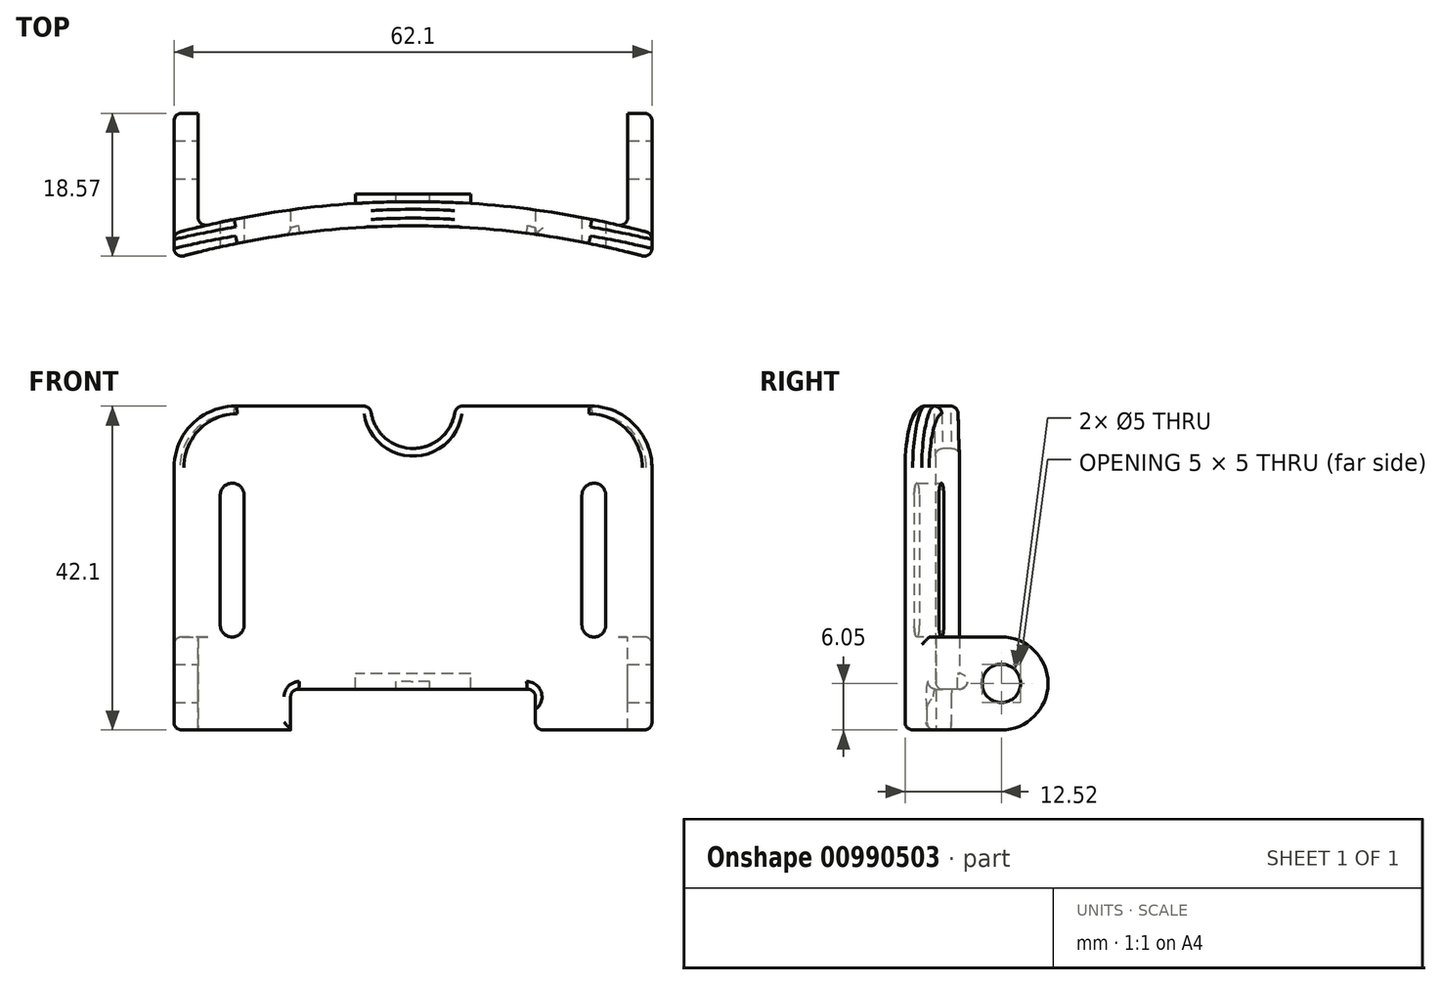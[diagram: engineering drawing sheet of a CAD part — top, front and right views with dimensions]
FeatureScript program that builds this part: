
annotation { "Feature Type Name" : "Feature", "Feature Type Description" : "" }
export const myFeature = defineFeature(function(context is Context, id is Id, definition is map)
    precondition{}
    {
        {
            var Q0;
            Q0=qCreatedBy(makeId("Top.planeOp"),FACE);
            var sketch = newSketch(context, id + "F0", { "sketchPlane" : qUnion([Q0])});
            skArc(sketch, "E0", {"start": v(8.06, 0) * mm, "mid": v(-23, 4.25) * mm, "end": v(-54.04, 0) * mm});
            skLineSegment(sketch, "E1", {"start": v(8.06, 0) * mm, "end": v(8.06, 18.88) * mm});
            skLineSegment(sketch, "E2", {"start": v(8.06, 18.88) * mm, "end": v(4.92, 18.88) * mm});
            skLineSegment(sketch, "E3", {"start": v(-54.04, 0) * mm, "end": v(-54.04, 18.88) * mm});
            skLineSegment(sketch, "E4", {"start": v(-54.04, 18.88) * mm, "end": v(-50.9, 18.88) * mm});
            skArc(sketch, "E5.0", {"start": v(8.06, 3.26) * mm, "mid": v(-23, 7.39) * mm, "end": v(-54.04, 3.26) * mm});
            skLineSegment(sketch, "E6", {"start": v(-50.9, 18.88) * mm, "end": v(-50.9, 4.06) * mm});
            skLineSegment(sketch, "E7", {"start": v(4.92, 18.88) * mm, "end": v(4.92, 4.06) * mm});
            skSolve(sketch);
        }
        {
            var Q0;
            Q0 = qSketchRegion(id + "F0", true);
            extrude(context, id + "F1", {"entities" : qUnion([Q0]), "depth" : 12.1 * mm, "offsetDistance" : 25 * mm});
        }
        {
            var Q0;
            {var subQ5=sQuery(id+"F0.wireOp",EDGE,"E0");Q0=makeQuery(id+"F0.imprint","IMPRINT",FACE,{"disambiguationData":[TD([[makeQuery(id+"F0.imprint","IMPRINT",EDGE,{"derivedFrom":subQ5}),-1.0]])]});}
            extrude(context, id + "F2", {"entities" : qUnion([Q0]), "operationType" : NewBodyOperationType.ADD, "depth" : 42.1 * mm, "offsetDistance" : 25 * mm});
        }
        {
            var Q0;
            Q0=makeQuery(id+"F1.opExtrude","CAP_EDGE",EDGE,{"disambiguationData":[OSD([sQuery(id+"F0.wireOp",EDGE,"E4")])],"isStart":false});
            var Q1;
            Q1=makeQuery(id+"F1.opExtrude","CAP_EDGE",EDGE,{"disambiguationData":[OSD([sQuery(id+"F0.wireOp",EDGE,"E4")])],"isStart":true});
            var Q2;
            Q2=makeQuery(id+"F1.opExtrude","CAP_EDGE",EDGE,{"disambiguationData":[OSD([sQuery(id+"F0.wireOp",EDGE,"E2")])],"isStart":true});
            var Q3;
            Q3=makeQuery(id+"F1.opExtrude","CAP_EDGE",EDGE,{"disambiguationData":[OSD([sQuery(id+"F0.wireOp",EDGE,"E2")])],"isStart":false});
            fillet(context, id + "F3", {"entities" : qUnion([Q0, Q1, Q2, Q3]), "radius" : 6.05 * mm, "tangentPropagation" : true, "allowEdgeOverflow" : false});
        }
        {
            var Q0;
            Q0=makeQuery(id+"F1.opExtrude","SWEPT_EDGE",EDGE,{"disambiguationData":[OSD([sQuery(id+"F0.wireOp",EDGE,"E5.0"),sQuery(id+"F0.wireOp",EDGE,"E7")])]});
            var Q1;
            Q1=makeQuery(id+"F1.opExtrude","SWEPT_EDGE",EDGE,{"disambiguationData":[OSD([sQuery(id+"F0.wireOp",EDGE,"E5.0"),sQuery(id+"F0.wireOp",EDGE,"E6")])]});
            var Q2;
            {var subQ0=sQuery(id+"F0.wireOp",EDGE,"E1");var subQ1=sQuery(id+"F0.wireOp",EDGE,"E0");Q2=makeQuery(id+"F2.boolean.opBoolean","MERGE",EDGE,{"derivedFrom":[makeQuery(id+"F1.opExtrude","SWEPT_EDGE",EDGE,{"disambiguationData":[OSD([subQ1,subQ0])]}),makeQuery(id+"F2.opExtrude","SWEPT_EDGE",EDGE,{"disambiguationData":[OSD([subQ1,subQ0])]})]});}
            var Q3;
            {var subQ0=sQuery(id+"F0.wireOp",EDGE,"E3");var subQ1=sQuery(id+"F0.wireOp",EDGE,"E0");Q3=makeQuery(id+"F2.boolean.opBoolean","MERGE",EDGE,{"derivedFrom":[makeQuery(id+"F1.opExtrude","SWEPT_EDGE",EDGE,{"disambiguationData":[OSD([subQ1,subQ0])]}),makeQuery(id+"F2.opExtrude","SWEPT_EDGE",EDGE,{"disambiguationData":[OSD([subQ1,subQ0])]})]});}
            var Q4;
            Q4=makeQuery(id+"F2.opExtrude","SWEPT_EDGE",EDGE,{"disambiguationData":[OSD([sQuery(id+"F0.wireOp",EDGE,"E1"),sQuery(id+"F0.wireOp",EDGE,"E5.0")])]});
            var Q5;
            Q5=makeQuery(id+"F2.opExtrude","SWEPT_EDGE",EDGE,{"disambiguationData":[OSD([sQuery(id+"F0.wireOp",EDGE,"E3"),sQuery(id+"F0.wireOp",EDGE,"E5.0")])]});
            var Q6;
            Q6=makeQuery(id+"F1.opExtrude","CAP_EDGE",EDGE,{"disambiguationData":[OSD([sQuery(id+"F0.wireOp",EDGE,"E3")])],"isStart":false});
            var Q7;
            {var subQ0=sQuery(id+"F0.wireOp",EDGE,"E1");Q7=makeQuery(id+"F3.opFillet","BLEND_EDGE",EDGE,{"blendedFrom":[makeQuery(id+"F1.opExtrude","CAP_EDGE",EDGE,{"disambiguationData":[OSD([sQuery(id+"F0.wireOp",EDGE,"E2")])],"isStart":true}),makeQuery(id+"F2.boolean.opBoolean","MERGE",FACE,{"derivedFrom":[makeQuery(id+"F1.opExtrude","SWEPT_FACE",FACE,{"disambiguationData":[OSD([subQ0])]}),makeQuery(id+"F2.opExtrude","SWEPT_FACE",FACE,{"disambiguationData":[OSD([subQ0])]})]})],"blendedInto":[makeQuery(id+"F2.boolean.opBoolean","MERGE",FACE,{"derivedFrom":[makeQuery(id+"F1.opExtrude","SWEPT_FACE",FACE,{"disambiguationData":[OSD([subQ0])]}),makeQuery(id+"F2.opExtrude","SWEPT_FACE",FACE,{"disambiguationData":[OSD([subQ0])]})]})]});}
            var Q8;
            Q8=makeQuery(id+"F2.opExtrude","CAP_EDGE",EDGE,{"disambiguationData":[OSD([sQuery(id+"F0.wireOp",EDGE,"E0")])],"isStart":false});
            var Q9;
            Q9=makeQuery(id+"F2.opExtrude","CAP_EDGE",EDGE,{"disambiguationData":[OSD([sQuery(id+"F0.wireOp",EDGE,"E5.0")])],"isStart":false});
            fillet(context, id + "F4", {"entities" : qUnion([Q0, Q1, Q2, Q3, Q4, Q5, Q6, Q7, Q8, Q9]), "radius" : 1 * mm, "tangentPropagation" : true, "allowEdgeOverflow" : false});
        }
        {
            var Q0;
            {var subQ0=sQuery(id+"F0.wireOp",EDGE,"E1");var subQ1=sQuery(id+"F0.wireOp",EDGE,"E0");Q0=makeQuery(id+"F4.opFillet","BLEND_VERTEX",VERTEX,{"blendedFrom":[makeQuery(id+"F2.boolean.opBoolean","MERGE",EDGE,{"derivedFrom":[makeQuery(id+"F1.opExtrude","SWEPT_EDGE",EDGE,{"disambiguationData":[OSD([subQ1,subQ0])]}),makeQuery(id+"F2.opExtrude","SWEPT_EDGE",EDGE,{"disambiguationData":[OSD([subQ1,subQ0])]})]}),makeQuery(id+"F2.boolean.opBoolean","MERGE",FACE,{"derivedFrom":[makeQuery(id+"F1.opExtrude","SWEPT_FACE",FACE,{"disambiguationData":[OSD([subQ1])]}),makeQuery(id+"F2.opExtrude","SWEPT_FACE",FACE,{"disambiguationData":[OSD([subQ1])]})]}),makeQuery(id+"F1.opExtrude","CAP_FACE",FACE,{"disambiguationData":[OSD([subQ1,subQ0,sQuery(id+"F0.wireOp",EDGE,"E2"),sQuery(id+"F0.wireOp",EDGE,"E3"),sQuery(id+"F0.wireOp",EDGE,"E4"),sQuery(id+"F0.wireOp",EDGE,"E5.0"),sQuery(id+"F0.wireOp",EDGE,"E6"),sQuery(id+"F0.wireOp",EDGE,"E7")])],"isStart":true})],"blendedInto":[makeQuery(id+"F2.boolean.opBoolean","MERGE",FACE,{"derivedFrom":[makeQuery(id+"F1.opExtrude","SWEPT_FACE",FACE,{"disambiguationData":[OSD([subQ1])]}),makeQuery(id+"F2.opExtrude","SWEPT_FACE",FACE,{"disambiguationData":[OSD([subQ1])]})]}),makeQuery(id+"F1.opExtrude","CAP_FACE",FACE,{"disambiguationData":[OSD([subQ1,subQ0,sQuery(id+"F0.wireOp",EDGE,"E2"),sQuery(id+"F0.wireOp",EDGE,"E3"),sQuery(id+"F0.wireOp",EDGE,"E4"),sQuery(id+"F0.wireOp",EDGE,"E5.0"),sQuery(id+"F0.wireOp",EDGE,"E6"),sQuery(id+"F0.wireOp",EDGE,"E7")])],"isStart":true})]});}
            var Q1;
            {var subQ0=sQuery(id+"F0.wireOp",EDGE,"E3");var subQ1=sQuery(id+"F0.wireOp",EDGE,"E0");Q1=makeQuery(id+"F4.opFillet","BLEND_VERTEX",VERTEX,{"blendedFrom":[makeQuery(id+"F2.boolean.opBoolean","MERGE",EDGE,{"derivedFrom":[makeQuery(id+"F1.opExtrude","SWEPT_EDGE",EDGE,{"disambiguationData":[OSD([subQ1,subQ0])]}),makeQuery(id+"F2.opExtrude","SWEPT_EDGE",EDGE,{"disambiguationData":[OSD([subQ1,subQ0])]})]}),makeQuery(id+"F2.boolean.opBoolean","MERGE",FACE,{"derivedFrom":[makeQuery(id+"F1.opExtrude","SWEPT_FACE",FACE,{"disambiguationData":[OSD([subQ1])]}),makeQuery(id+"F2.opExtrude","SWEPT_FACE",FACE,{"disambiguationData":[OSD([subQ1])]})]}),makeQuery(id+"F1.opExtrude","CAP_FACE",FACE,{"disambiguationData":[OSD([subQ1,sQuery(id+"F0.wireOp",EDGE,"E1"),sQuery(id+"F0.wireOp",EDGE,"E2"),subQ0,sQuery(id+"F0.wireOp",EDGE,"E4"),sQuery(id+"F0.wireOp",EDGE,"E5.0"),sQuery(id+"F0.wireOp",EDGE,"E6"),sQuery(id+"F0.wireOp",EDGE,"E7")])],"isStart":true})],"blendedInto":[makeQuery(id+"F2.boolean.opBoolean","MERGE",FACE,{"derivedFrom":[makeQuery(id+"F1.opExtrude","SWEPT_FACE",FACE,{"disambiguationData":[OSD([subQ1])]}),makeQuery(id+"F2.opExtrude","SWEPT_FACE",FACE,{"disambiguationData":[OSD([subQ1])]})]}),makeQuery(id+"F1.opExtrude","CAP_FACE",FACE,{"disambiguationData":[OSD([subQ1,sQuery(id+"F0.wireOp",EDGE,"E1"),sQuery(id+"F0.wireOp",EDGE,"E2"),subQ0,sQuery(id+"F0.wireOp",EDGE,"E4"),sQuery(id+"F0.wireOp",EDGE,"E5.0"),sQuery(id+"F0.wireOp",EDGE,"E6"),sQuery(id+"F0.wireOp",EDGE,"E7")])],"isStart":true})]});}
            var Q2;
            {var subQ0=sQuery(id+"F0.wireOp",EDGE,"E0");var subQ1=sQuery(id+"F0.wireOp",EDGE,"E3");Q2=makeQuery(id+"F4.opFillet","BLEND_VERTEX",VERTEX,{"blendedFrom":[makeQuery(id+"F2.opExtrude","CAP_EDGE",EDGE,{"disambiguationData":[OSD([subQ0])],"isStart":false}),makeQuery(id+"F2.boolean.opBoolean","MERGE",EDGE,{"derivedFrom":[makeQuery(id+"F1.opExtrude","SWEPT_EDGE",EDGE,{"disambiguationData":[OSD([subQ0,subQ1])]}),makeQuery(id+"F2.opExtrude","SWEPT_EDGE",EDGE,{"disambiguationData":[OSD([subQ0,subQ1])]})]}),makeQuery(id+"F2.boolean.opBoolean","MERGE",FACE,{"derivedFrom":[makeQuery(id+"F1.opExtrude","SWEPT_FACE",FACE,{"disambiguationData":[OSD([subQ0])]}),makeQuery(id+"F2.opExtrude","SWEPT_FACE",FACE,{"disambiguationData":[OSD([subQ0])]})]})],"blendedInto":[makeQuery(id+"F2.boolean.opBoolean","MERGE",FACE,{"derivedFrom":[makeQuery(id+"F1.opExtrude","SWEPT_FACE",FACE,{"disambiguationData":[OSD([subQ0])]}),makeQuery(id+"F2.opExtrude","SWEPT_FACE",FACE,{"disambiguationData":[OSD([subQ0])]})]})]});}
            cPlane(context, id + "F5", {"entities" : qUnion([Q0, Q1, Q2]), "cplaneType" : CPlaneType.THREE_POINT, "offset" : 25 * mm, "width" : 150 * mm, "height" : 150 * mm});
        }
        {
            var Q0;
            Q0=qCreatedBy(id+"F5.planeOp",FACE);
            var sketch = newSketch(context, id + "F6", { "sketchPlane" : qUnion([Q0])});
            skPoint(sketch, "E8.0", {"position": v(-23, 0) * mm});
            skLineSegment(sketch, "E9.0", {"start": v(-54.04, 0) * mm, "end": v(-54.04, 42.1) * mm, "construction": true});
            skLineSegment(sketch, "E10.0", {"start": v(8.06, 42.1) * mm, "end": v(8.06, 0) * mm, "construction": true});
            skLineSegment(sketch, "E11", {"start": v(-23, 42.1) * mm, "end": v(-23, 0) * mm, "construction": true});
            skLineSegment(sketch, "E12.bottom", {"start": v(-7.1, 0) * mm, "end": v(-38.9, 0) * mm});
            skLineSegment(sketch, "E12.top", {"start": v(-7.1, 5.3) * mm, "end": v(-38.9, 5.3) * mm});
            skLineSegment(sketch, "E12.left", {"start": v(-7.1, 0) * mm, "end": v(-7.1, 5.3) * mm});
            skLineSegment(sketch, "E12.right", {"start": v(-38.9, 0) * mm, "end": v(-38.9, 5.3) * mm});
            skLineSegment(sketch, "E13.bottom", {"start": v(2.06, 32.08) * mm, "end": v(-1.04, 32.08) * mm});
            skLineSegment(sketch, "E13.top", {"start": v(2.06, 12.08) * mm, "end": v(-1.04, 12.08) * mm});
            skLineSegment(sketch, "E13.left", {"start": v(2.06, 32.08) * mm, "end": v(2.06, 12.08) * mm});
            skLineSegment(sketch, "E13.right", {"start": v(-1.04, 32.08) * mm, "end": v(-1.04, 12.08) * mm});
            skLineSegment(sketch, "E14.MirrorCS", {"start": v(-48.04, 32.08) * mm, "end": v(-48.04, 12.08) * mm});
            skLineSegment(sketch, "E15.MirrorCS", {"start": v(-44.94, 32.08) * mm, "end": v(-44.94, 12.08) * mm});
            skLineSegment(sketch, "E16.MirrorCS", {"start": v(-48.04, 12.08) * mm, "end": v(-44.94, 12.08) * mm});
            skLineSegment(sketch, "E17.MirrorCS", {"start": v(-48.04, 32.08) * mm, "end": v(-44.94, 32.08) * mm});
            skCircle(sketch, "E18", {"center": v(-23, 42.1) * mm, "radius": 5.5 * mm});
            skSolve(sketch);
        }
        {
            var Q0;
            Q0 = qSketchRegion(id + "F6", true);
            extrude(context, id + "F7", {"entities" : qUnion([Q0]), "operationType" : NewBodyOperationType.REMOVE, "endBound" : BoundingType.THROUGH_ALL, "oppositeDirection" : true, "depth" : 25 * mm, "offsetDistance" : 25 * mm});
        }
        {
            var Q0;
            Q0=makeQuery(id+"F7.boolean.opBoolean","COPY",EDGE,{"derivedFrom":makeQuery(id+"F7.opExtrude","SWEPT_EDGE",EDGE,{"disambiguationData":[OSD([sQuery(id+"F6.wireOp",EDGE,"E12.bottom"),sQuery(id+"F6.wireOp",EDGE,"E12.left")])]})});
            var Q1;
            Q1=makeQuery(id+"F7.boolean.opBoolean","COPY",EDGE,{"derivedFrom":makeQuery(id+"F7.opExtrude","SWEPT_EDGE",EDGE,{"disambiguationData":[OSD([sQuery(id+"F6.wireOp",EDGE,"E12.top"),sQuery(id+"F6.wireOp",EDGE,"E12.left")])]})});
            var Q2;
            Q2=makeQuery(id+"F7.boolean.opBoolean","COPY",EDGE,{"derivedFrom":makeQuery(id+"F7.opExtrude","SWEPT_EDGE",EDGE,{"disambiguationData":[OSD([sQuery(id+"F6.wireOp",EDGE,"E12.top"),sQuery(id+"F6.wireOp",EDGE,"E12.right")])]})});
            var Q3;
            Q3=makeQuery(id+"F7.boolean.opBoolean","COPY",EDGE,{"derivedFrom":makeQuery(id+"F7.opExtrude","SWEPT_EDGE",EDGE,{"disambiguationData":[OSD([sQuery(id+"F6.wireOp",EDGE,"E12.bottom"),sQuery(id+"F6.wireOp",EDGE,"E12.right")])]})});
            var Q4;
            Q4=makeQuery(id+"F7.boolean.opBoolean","INTERSECT",EDGE,{"disambiguationData":[OD(0.0)],"derivedFrom":[makeQuery(id+"F2.opExtrude","CAP_FACE",FACE,{"disambiguationData":[OSD([sQuery(id+"F0.wireOp",EDGE,"E0"),sQuery(id+"F0.wireOp",EDGE,"E1"),sQuery(id+"F0.wireOp",EDGE,"E3"),sQuery(id+"F0.wireOp",EDGE,"E5.0")])],"isStart":false}),makeQuery(id+"F7.opExtrude","SWEPT_FACE",FACE,{"disambiguationData":[OSD([sQuery(id+"F6.wireOp",EDGE,"E18")])]})]});
            var Q5;
            Q5=makeQuery(id+"F7.boolean.opBoolean","INTERSECT",EDGE,{"disambiguationData":[OD(1.0)],"derivedFrom":[makeQuery(id+"F2.opExtrude","CAP_FACE",FACE,{"disambiguationData":[OSD([sQuery(id+"F0.wireOp",EDGE,"E0"),sQuery(id+"F0.wireOp",EDGE,"E1"),sQuery(id+"F0.wireOp",EDGE,"E3"),sQuery(id+"F0.wireOp",EDGE,"E5.0")])],"isStart":false}),makeQuery(id+"F7.opExtrude","SWEPT_FACE",FACE,{"disambiguationData":[OSD([sQuery(id+"F6.wireOp",EDGE,"E18")])]})]});
            var Q6;
            {var subQ1=sQuery(id+"F0.wireOp",EDGE,"E0");Q6=makeQuery(id+"F7.boolean.opBoolean","SPLIT",EDGE,{"disambiguationData":[TD([makeQuery(id+"F7.opExtrude","SWEPT_FACE",FACE,{"disambiguationData":[OSD([sQuery(id+"F6.wireOp",EDGE,"E12.right")])]})])],"derivedFrom":makeQuery(id+"F1.opExtrude","CAP_EDGE",EDGE,{"disambiguationData":[OSD([subQ1])],"isStart":true})});}
            var Q7;
            {var subQ0=sQuery(id+"F0.wireOp",EDGE,"E0");Q7=makeQuery(id+"F7.boolean.opBoolean","INTERSECT",EDGE,{"derivedFrom":[makeQuery(id+"F2.boolean.opBoolean","MERGE",FACE,{"derivedFrom":[makeQuery(id+"F1.opExtrude","SWEPT_FACE",FACE,{"disambiguationData":[OSD([subQ0])]}),makeQuery(id+"F2.opExtrude","SWEPT_FACE",FACE,{"disambiguationData":[OSD([subQ0])]})]}),makeQuery(id+"F7.opExtrude","SWEPT_FACE",FACE,{"disambiguationData":[OSD([sQuery(id+"F6.wireOp",EDGE,"E12.right")])]})]});}
            var Q8;
            {var subQ0=sQuery(id+"F0.wireOp",EDGE,"E0");Q8=makeQuery(id+"F7.boolean.opBoolean","INTERSECT",EDGE,{"derivedFrom":[makeQuery(id+"F2.boolean.opBoolean","MERGE",FACE,{"derivedFrom":[makeQuery(id+"F1.opExtrude","SWEPT_FACE",FACE,{"disambiguationData":[OSD([subQ0])]}),makeQuery(id+"F2.opExtrude","SWEPT_FACE",FACE,{"disambiguationData":[OSD([subQ0])]})]}),makeQuery(id+"F7.opExtrude","SWEPT_FACE",FACE,{"disambiguationData":[OSD([sQuery(id+"F6.wireOp",EDGE,"E12.top")])]})]});}
            var Q9;
            {var subQ1=sQuery(id+"F0.wireOp",EDGE,"E0");Q9=makeQuery(id+"F7.boolean.opBoolean","SPLIT",EDGE,{"disambiguationData":[TD([makeQuery(id+"F7.opExtrude","SWEPT_FACE",FACE,{"disambiguationData":[OSD([sQuery(id+"F6.wireOp",EDGE,"E12.left")])]})])],"derivedFrom":makeQuery(id+"F1.opExtrude","CAP_EDGE",EDGE,{"disambiguationData":[OSD([subQ1])],"isStart":true})});}
            fillet(context, id + "F8", {"entities" : qUnion([Q0, Q1, Q2, Q3, Q4, Q5, Q6, Q7, Q8, Q9]), "radius" : 1 * mm, "tangentPropagation" : true, "allowEdgeOverflow" : false});
        }
        {
            var Q0;
            Q0=makeQuery(id+"F7.boolean.opBoolean","COPY",EDGE,{"derivedFrom":makeQuery(id+"F7.opExtrude","SWEPT_EDGE",EDGE,{"disambiguationData":[OSD([sQuery(id+"F6.wireOp",EDGE,"E15.MirrorCS"),sQuery(id+"F6.wireOp",EDGE,"E17.MirrorCS")])]})});
            var Q1;
            Q1=makeQuery(id+"F7.boolean.opBoolean","COPY",EDGE,{"derivedFrom":makeQuery(id+"F7.opExtrude","SWEPT_EDGE",EDGE,{"disambiguationData":[OSD([sQuery(id+"F6.wireOp",EDGE,"E13.bottom"),sQuery(id+"F6.wireOp",EDGE,"E13.left")])]})});
            var Q2;
            Q2=makeQuery(id+"F7.boolean.opBoolean","COPY",EDGE,{"derivedFrom":makeQuery(id+"F7.opExtrude","SWEPT_EDGE",EDGE,{"disambiguationData":[OSD([sQuery(id+"F6.wireOp",EDGE,"E13.bottom"),sQuery(id+"F6.wireOp",EDGE,"E13.right")])]})});
            var Q3;
            Q3=makeQuery(id+"F7.boolean.opBoolean","COPY",EDGE,{"derivedFrom":makeQuery(id+"F7.opExtrude","SWEPT_EDGE",EDGE,{"disambiguationData":[OSD([sQuery(id+"F6.wireOp",EDGE,"E14.MirrorCS"),sQuery(id+"F6.wireOp",EDGE,"E17.MirrorCS")])]})});
            var Q4;
            Q4=makeQuery(id+"F7.boolean.opBoolean","COPY",EDGE,{"derivedFrom":makeQuery(id+"F7.opExtrude","SWEPT_EDGE",EDGE,{"disambiguationData":[OSD([sQuery(id+"F6.wireOp",EDGE,"E15.MirrorCS"),sQuery(id+"F6.wireOp",EDGE,"E16.MirrorCS")])]})});
            var Q5;
            Q5=makeQuery(id+"F7.boolean.opBoolean","COPY",EDGE,{"derivedFrom":makeQuery(id+"F7.opExtrude","SWEPT_EDGE",EDGE,{"disambiguationData":[OSD([sQuery(id+"F6.wireOp",EDGE,"E13.top"),sQuery(id+"F6.wireOp",EDGE,"E13.left")])]})});
            var Q6;
            Q6=makeQuery(id+"F7.boolean.opBoolean","COPY",EDGE,{"derivedFrom":makeQuery(id+"F7.opExtrude","SWEPT_EDGE",EDGE,{"disambiguationData":[OSD([sQuery(id+"F6.wireOp",EDGE,"E13.top"),sQuery(id+"F6.wireOp",EDGE,"E13.right")])]})});
            var Q7;
            Q7=makeQuery(id+"F7.boolean.opBoolean","COPY",EDGE,{"derivedFrom":makeQuery(id+"F7.opExtrude","SWEPT_EDGE",EDGE,{"disambiguationData":[OSD([sQuery(id+"F6.wireOp",EDGE,"E14.MirrorCS"),sQuery(id+"F6.wireOp",EDGE,"E16.MirrorCS")])]})});
            fillet(context, id + "F9", {"entities" : qUnion([Q0, Q1, Q2, Q3, Q4, Q5, Q6, Q7]), "radius" : 1.55 * mm, "tangentPropagation" : true, "allowEdgeOverflow" : false});
        }
        {
            var Q0;
            Q0=makeQuery(id+"F1.opExtrude","SWEPT_FACE",FACE,{"disambiguationData":[OSD([sQuery(id+"F0.wireOp",EDGE,"E7")])]});
            var sketch = newSketch(context, id + "F10", { "sketchPlane" : qUnion([Q0])});
            skPoint(sketch, "E19.0", {"position": v(-18.88, 6.05) * mm});
            skLineSegment(sketch, "E20", {"start": v(-18.88, 6.05) * mm, "end": v(2.29, 6.05) * mm, "construction": true});
            skCircle(sketch, "E21", {"center": v(-12.83, 6.05) * mm, "radius": 2.5 * mm});
            skSolve(sketch);
        }
        {
            var Q0;
            Q0 = qSketchRegion(id + "F10", true);
            extrude(context, id + "F11", {"entities" : qUnion([Q0]), "operationType" : NewBodyOperationType.REMOVE, "endBound" : BoundingType.SYMMETRIC, "depth" : 153.6 * mm, "offsetDistance" : 25 * mm});
        }
        {
            var Q0;
            Q0=makeQuery(id+"F2.opExtrude","CAP_EDGE",EDGE,{"disambiguationData":[OSD([sQuery(id+"F0.wireOp",EDGE,"E3")])],"isStart":false});
            var Q1;
            Q1=makeQuery(id+"F2.opExtrude","CAP_EDGE",EDGE,{"disambiguationData":[OSD([sQuery(id+"F0.wireOp",EDGE,"E1")])],"isStart":false});
            fillet(context, id + "F12", {"entities" : qUnion([Q0, Q1]), "radius" : 8 * mm, "tangentPropagation" : true, "allowEdgeOverflow" : false});
        }
        {
            var Q0;
            {var subQ0=sQuery(id+"F0.wireOp",EDGE,"E5.0");Q0=makeQuery(id+"F8.opFillet","BLEND_EDGE",EDGE,{"blendedFrom":[makeQuery(id+"F7.boolean.opBoolean","COPY",EDGE,{"derivedFrom":makeQuery(id+"F7.opExtrude","SWEPT_EDGE",EDGE,{"disambiguationData":[OSD([sQuery(id+"F6.wireOp",EDGE,"E12.top"),sQuery(id+"F6.wireOp",EDGE,"E12.left")])]})}),makeQuery(id+"F2.boolean.opBoolean","MERGE",FACE,{"derivedFrom":[makeQuery(id+"F1.opExtrude","SWEPT_FACE",FACE,{"disambiguationData":[OSD([subQ0])]}),makeQuery(id+"F2.opExtrude","SWEPT_FACE",FACE,{"disambiguationData":[OSD([subQ0])]})]})],"blendedInto":[makeQuery(id+"F2.boolean.opBoolean","MERGE",FACE,{"derivedFrom":[makeQuery(id+"F1.opExtrude","SWEPT_FACE",FACE,{"disambiguationData":[OSD([subQ0])]}),makeQuery(id+"F2.opExtrude","SWEPT_FACE",FACE,{"disambiguationData":[OSD([subQ0])]})]})]});}
            cPoint(context, id + "F13", {"entities" : qUnion([Q0]), "parameter" : 0.5});
        }
        {
            var Q0;
            {var subQ0=sQuery(id+"F0.wireOp",EDGE,"E5.0");Q0=makeQuery(id+"F8.opFillet","BLEND_EDGE",EDGE,{"blendedFrom":[makeQuery(id+"F7.boolean.opBoolean","COPY",EDGE,{"derivedFrom":makeQuery(id+"F7.opExtrude","SWEPT_EDGE",EDGE,{"disambiguationData":[OSD([sQuery(id+"F6.wireOp",EDGE,"E12.top"),sQuery(id+"F6.wireOp",EDGE,"E12.right")])]})}),makeQuery(id+"F2.boolean.opBoolean","MERGE",FACE,{"derivedFrom":[makeQuery(id+"F1.opExtrude","SWEPT_FACE",FACE,{"disambiguationData":[OSD([subQ0])]}),makeQuery(id+"F2.opExtrude","SWEPT_FACE",FACE,{"disambiguationData":[OSD([subQ0])]})]})],"blendedInto":[makeQuery(id+"F2.boolean.opBoolean","MERGE",FACE,{"derivedFrom":[makeQuery(id+"F1.opExtrude","SWEPT_FACE",FACE,{"disambiguationData":[OSD([subQ0])]}),makeQuery(id+"F2.opExtrude","SWEPT_FACE",FACE,{"disambiguationData":[OSD([subQ0])]})]})]});}
            cPoint(context, id + "F14", {"entities" : qUnion([Q0]), "parameter" : 0.5});
        }
        {
            var Q0;
            {var subQ0=sQuery(id+"F0.wireOp",EDGE,"E5.0");var subQ1=makeQuery(id+"F2.boolean.opBoolean","MERGE",FACE,{"derivedFrom":[makeQuery(id+"F1.opExtrude","SWEPT_FACE",FACE,{"disambiguationData":[OSD([subQ0])]}),makeQuery(id+"F2.opExtrude","SWEPT_FACE",FACE,{"disambiguationData":[OSD([subQ0])]})]});Q0=makeQuery(id+"F8.opFillet","BLEND_EDGE",EDGE,{"blendedFrom":[makeQuery(id+"F7.boolean.opBoolean","INTERSECT",EDGE,{"derivedFrom":[subQ1,makeQuery(id+"F7.opExtrude","SWEPT_FACE",FACE,{"disambiguationData":[OSD([sQuery(id+"F6.wireOp",EDGE,"E18")])]})]}),subQ1],"blendedInto":[subQ1]});}
            cPoint(context, id + "F15", {"entities" : qUnion([Q0]), "parameter" : 0.5});
        }
        {
            var Q0;
            Q0 = qCreatedBy(id + "F13" ,VERTEX);
            var Q1;
            Q1 = qCreatedBy(id + "F14" ,VERTEX);
            var Q2;
            Q2 = qCreatedBy(id + "F15" ,VERTEX);
            cPlane(context, id + "F16", {"entities" : qUnion([Q0, Q1, Q2]), "cplaneType" : CPlaneType.THREE_POINT, "offset" : 25 * mm, "width" : 150 * mm, "height" : 150 * mm});
        }
        {
            var Q0;
            Q0=qCreatedBy(id+"F16.planeOp",FACE);
            var sketch = newSketch(context, id + "F17", { "sketchPlane" : qUnion([Q0])});
            skPoint(sketch, "E22.0", {"position": v(-23, 5.55) * mm});
            skLineSegment(sketch, "E23", {"start": v(-23, 5.55) * mm, "end": v(-23, 17.05) * mm, "construction": true});
            skLineSegment(sketch, "E24.bottom", {"start": v(-15.5, 5.55) * mm, "end": v(-30.5, 5.55) * mm});
            skLineSegment(sketch, "E24.top", {"start": v(-15.5, 7.55) * mm, "end": v(-30.5, 7.55) * mm});
            skLineSegment(sketch, "E24.left", {"start": v(-15.5, 5.55) * mm, "end": v(-15.5, 7.55) * mm});
            skLineSegment(sketch, "E24.right", {"start": v(-30.5, 5.55) * mm, "end": v(-30.5, 7.55) * mm});
            skSolve(sketch);
        }
        {
            var Q0;
            Q0 = qSketchRegion(id + "F17", true);
            extrude(context, id + "F18", {"entities" : qUnion([Q0]), "operationType" : NewBodyOperationType.ADD, "oppositeDirection" : true, "depth" : 2 * mm, "offsetDistance" : 25 * mm});
        }
        {
            var Q0;
            Q0=makeQuery(id+"F18.opExtrude","CAP_EDGE",EDGE,{"disambiguationData":[OSD([sQuery(id+"F17.wireOp",EDGE,"E24.bottom")])],"isStart":false});
            var Q1;
            Q1=makeQuery(id+"F18.opExtrude","CAP_EDGE",EDGE,{"disambiguationData":[OSD([sQuery(id+"F17.wireOp",EDGE,"E24.top")])],"isStart":false});
            fillet(context, id + "F19", {"entities" : qUnion([Q0, Q1]), "radius" : 1 * mm, "tangentPropagation" : true, "allowEdgeOverflow" : false});
        }
    });
